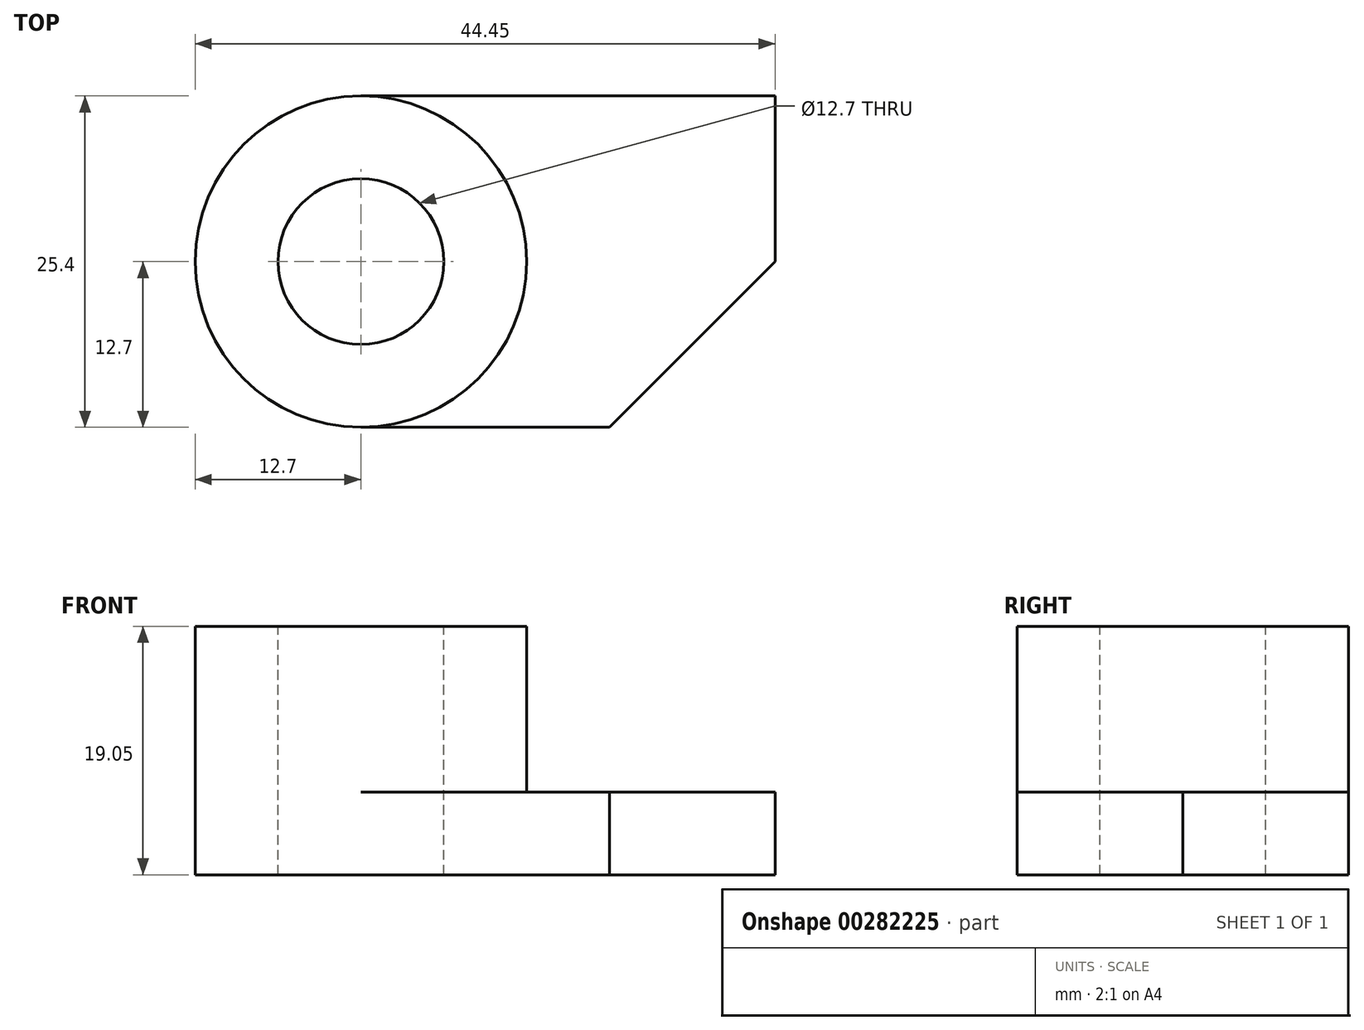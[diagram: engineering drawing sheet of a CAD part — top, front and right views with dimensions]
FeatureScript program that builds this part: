
annotation { "Feature Type Name" : "Feature", "Feature Type Description" : "" }
export const myFeature = defineFeature(function(context is Context, id is Id, definition is map)
    precondition{}
    {
        {
            var Q0;
            Q0=qCreatedBy(makeId("Top.planeOp"),FACE);
            var sketch = newSketch(context, id + "F0", { "sketchPlane" : qUnion([Q0])});
            skCircle(sketch, "E0", {"center": v(0, 0) * mm, "radius": 12.7 * mm});
            skLineSegment(sketch, "E1.bottom", {"start": v(0, 12.7) * mm, "end": v(31.75, 12.7) * mm});
            skLineSegment(sketch, "E1.top", {"start": v(0, -12.7) * mm, "end": v(31.75, -12.7) * mm});
            skLineSegment(sketch, "E1.right", {"start": v(31.75, 12.7) * mm, "end": v(31.75, -12.7) * mm});
            skSolve(sketch);
        }
        {
            var Q0;
            {var subQ0=sQuery(id+"F0.wireOp",EDGE,"E0");var subQ1=makeQuery(id+"F0.imprint","INTERSECT",VERTEX,{"derivedFrom":[subQ0,sQuery(id+"F0.wireOp",EDGE,"E1.bottom")]});Q0=makeQuery(id+"F0.imprint","IMPRINT",FACE,{"disambiguationData":[TD([[makeQuery(id+"F0.imprint","IMPRINT",EDGE,{"disambiguationData":[TD([[subQ1,-1.0]])],"derivedFrom":subQ0}),1.0]])]});}
            extrude(context, id + "F1", {"entities" : qUnion([Q0]), "depth" : 19.05 * mm});
        }
        {
            var Q0;
            {var subQ0=sQuery(id+"F0.wireOp",EDGE,"E1.bottom");Q0=makeQuery(id+"F0.imprint","IMPRINT",FACE,{"disambiguationData":[TD([[makeQuery(id+"F0.imprint","IMPRINT",EDGE,{"derivedFrom":subQ0}),-1.0]])]});}
            extrude(context, id + "F2", {"entities" : qUnion([Q0]), "operationType" : NewBodyOperationType.ADD, "depth" : 6.35 * mm});
        }
        {
            var Q0;
            Q0=makeQuery(id+"F1.opExtrude","CAP_FACE",FACE,{"disambiguationData":[OSD([sQuery(id+"F0.wireOp",EDGE,"E0")])],"isStart":false});
            var sketch = newSketch(context, id + "F3", { "sketchPlane" : qUnion([Q0])});
            skCircle(sketch, "E2", {"center": v(0, 0) * mm, "radius": 6.35 * mm});
            skSolve(sketch);
        }
        {
            var Q0;
            Q0=makeQuery(id+"F3.imprint","IMPRINT",FACE,{"disambiguationData":[TD([[makeQuery(id+"F3.imprint","IMPRINT",EDGE,{"derivedFrom":sQuery(id+"F3.wireOp",EDGE,"E2")}),1.0]])]});
            extrude(context, id + "F4", {"entities" : qUnion([Q0]), "operationType" : NewBodyOperationType.REMOVE, "endBound" : BoundingType.THROUGH_ALL, "oppositeDirection" : true, "depth" : 25.4 * mm});
        }
        {
            var Q0;
            Q0=makeQuery(id+"F2.opExtrude","CAP_FACE",FACE,{"disambiguationData":[OSD([sQuery(id+"F0.wireOp",EDGE,"E0"),sQuery(id+"F0.wireOp",EDGE,"E1.bottom"),sQuery(id+"F0.wireOp",EDGE,"E1.top"),sQuery(id+"F0.wireOp",EDGE,"E1.right")])],"isStart":false});
            var sketch = newSketch(context, id + "F5", { "sketchPlane" : qUnion([Q0])});
            skLineSegment(sketch, "E3", {"start": v(19.05, -12.7) * mm, "end": v(31.75, 0) * mm});
            skLineSegment(sketch, "E4", {"start": v(31.75, 0) * mm, "end": v(31.75, -12.7) * mm});
            skLineSegment(sketch, "E5", {"start": v(31.75, -12.7) * mm, "end": v(19.05, -12.7) * mm});
            skSolve(sketch);
        }
        {
            var Q0;
            Q0 = qSketchRegion(id + "F5", true);
            extrude(context, id + "F6", {"entities" : qUnion([Q0]), "operationType" : NewBodyOperationType.REMOVE, "oppositeDirection" : true, "depth" : 6.35 * mm});
        }
    });
